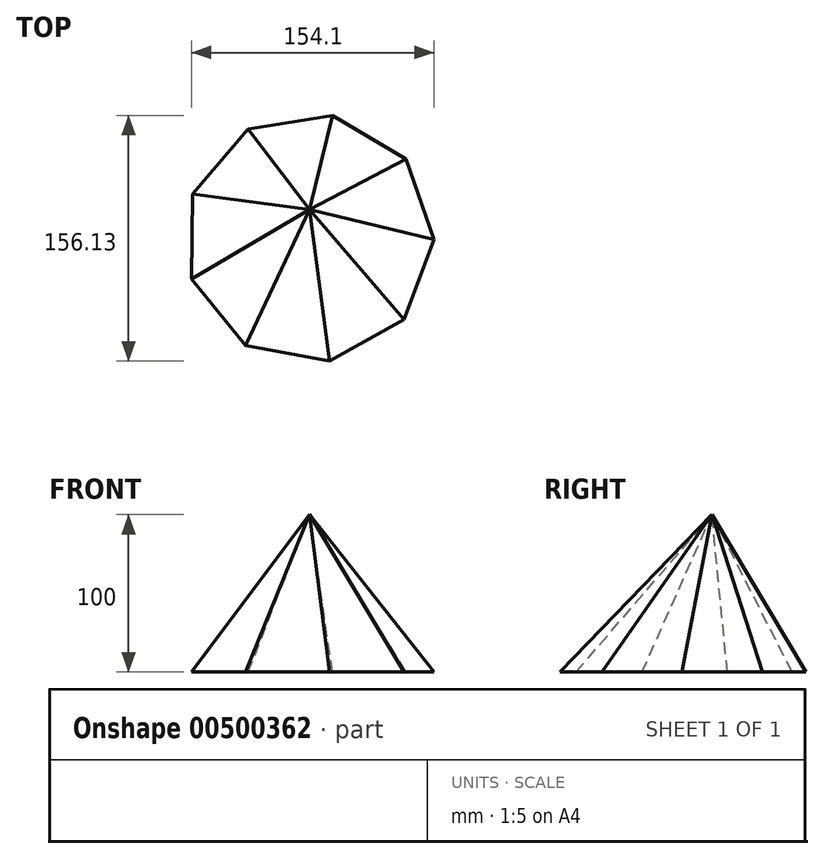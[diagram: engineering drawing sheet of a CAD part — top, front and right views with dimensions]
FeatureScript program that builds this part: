
annotation { "Feature Type Name" : "Feature", "Feature Type Description" : "" }
export const myFeature = defineFeature(function(context is Context, id is Id, definition is map)
    precondition{}
    {
        {
            var Q0;
            Q0=qCreatedBy(makeId("Top.planeOp"),FACE);
            var sketch = newSketch(context, id + "F0", { "sketchPlane" : qUnion([Q0])});
            skCircle(sketch, "E0.cCircle", {"center": v(0, 0) * mm, "radius": 74.5 * mm, "construction": true});
            skLineSegment(sketch, "E0.0", {"start": v(60.09, -51.72) * mm, "end": v(12.78, -78.24) * mm});
            skLineSegment(sketch, "E0.1", {"start": v(12.78, -78.24) * mm, "end": v(-40.5, -68.15) * mm});
            skLineSegment(sketch, "E0.2", {"start": v(-40.5, -68.15) * mm, "end": v(-74.83, -26.18) * mm});
            skLineSegment(sketch, "E0.3", {"start": v(-74.83, -26.18) * mm, "end": v(-74.15, 28.05) * mm});
            skLineSegment(sketch, "E0.4", {"start": v(-74.15, 28.05) * mm, "end": v(-38.77, 69.15) * mm});
            skLineSegment(sketch, "E0.5", {"start": v(-38.77, 69.15) * mm, "end": v(14.75, 77.9) * mm});
            skLineSegment(sketch, "E0.6", {"start": v(14.75, 77.9) * mm, "end": v(61.37, 50.2) * mm});
            skLineSegment(sketch, "E0.7", {"start": v(61.37, 50.2) * mm, "end": v(79.27, -1) * mm});
            skLineSegment(sketch, "E0.8", {"start": v(79.27, -1) * mm, "end": v(60.09, -51.72) * mm});
            skPoint(sketch, "E0.0.midPoint", {"position": v(36.43, -64.98) * mm});
            skSolve(sketch);
        }
        {
            var Q0;
            Q0=qCreatedBy(makeId("Top.planeOp"),FACE);
            cPlane(context, id + "F1", {"entities" : qUnion([Q0]), "cplaneType" : CPlaneType.OFFSET, "offset" : 100 * mm, "width" : 150 * mm, "height" : 150 * mm});
        }
        {
            var Q0;
            Q0=qCreatedBy(id+"F1.planeOp",FACE);
            var sketch = newSketch(context, id + "F2", { "sketchPlane" : qUnion([Q0])});
            skPoint(sketch, "E1", {"position": v(0, 18.19) * mm});
            skSolve(sketch);
        }
        {
            var Q0;
            Q0=makeQuery(id+"F0.imprint","IMPRINT",FACE,{"disambiguationData":[TD([[makeQuery(id+"F0.imprint","IMPRINT",EDGE,{"derivedFrom":sQuery(id+"F0.wireOp",EDGE,"E0.0")}),-1.0]])]});
            var Q1;
            Q1=sQuery(id+"F2.wireOp",VERTEX,"E1");
            loft(context, id + "F3", {"sheetProfilesArray" : [{ "sheetProfileEntities" : qUnion([Q0]) }, { "sheetProfileEntities" : qUnion([Q1]) }]});
        }
    });
